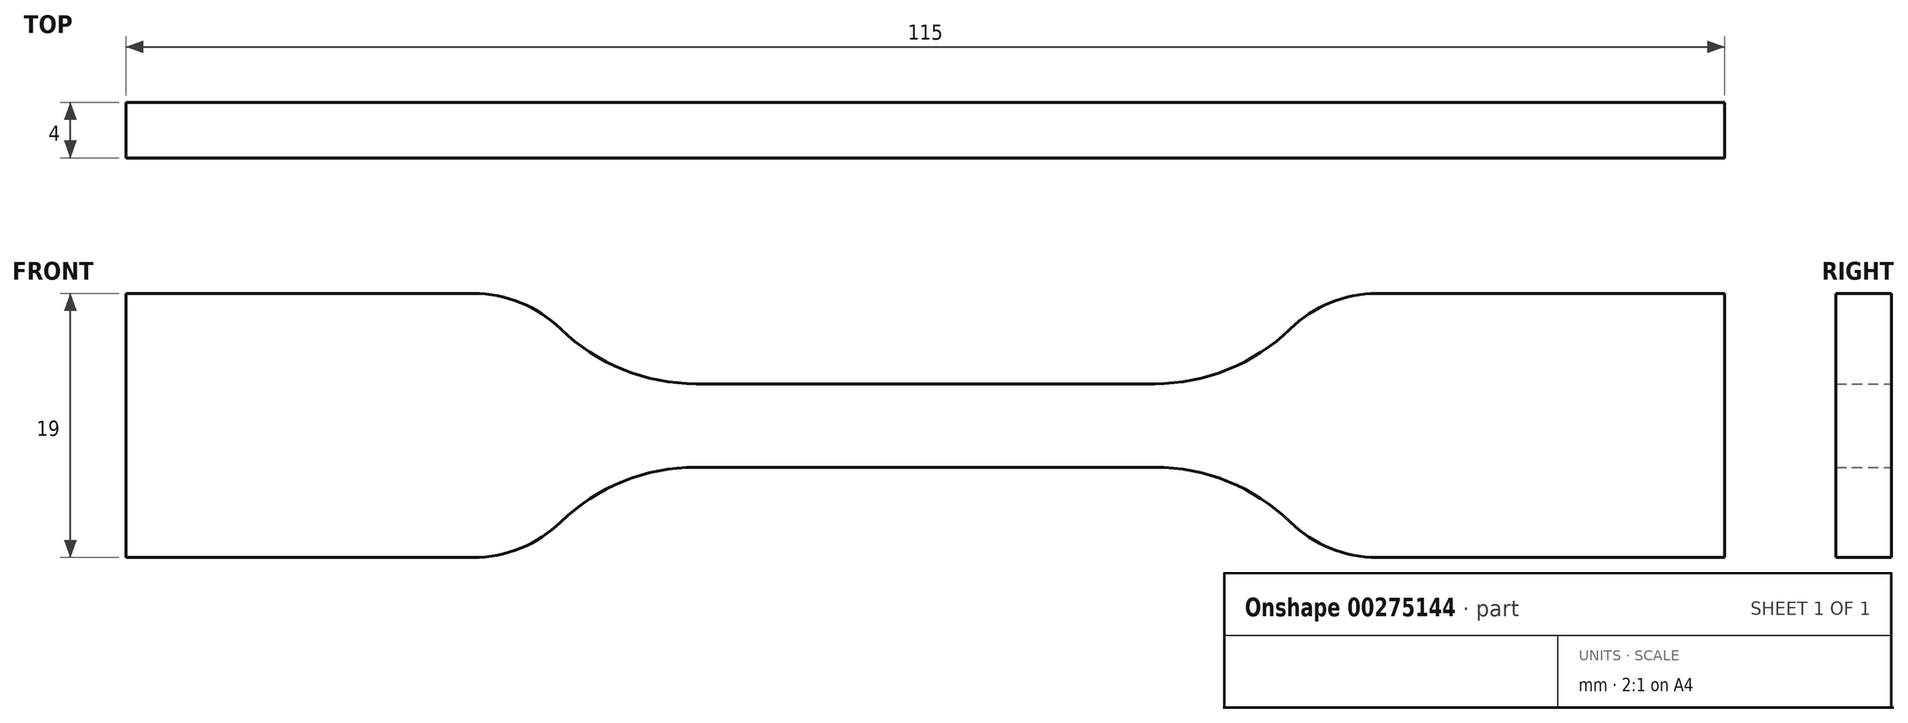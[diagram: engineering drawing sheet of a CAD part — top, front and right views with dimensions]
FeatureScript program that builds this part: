
annotation { "Feature Type Name" : "Feature", "Feature Type Description" : "" }
export const myFeature = defineFeature(function(context is Context, id is Id, definition is map)
    precondition{}
    {
        {
            var Q0;
            Q0=qCreatedBy(makeId("Front.planeOp"),FACE);
            var sketch = newSketch(context, id + "F0", { "sketchPlane" : qUnion([Q0])});
            skLineSegment(sketch, "E0", {"start": v(0, 3) * mm, "end": v(16.5, 3) * mm});
            skArc(sketch, "E1", {"start": v(16.5, 3) * mm, "mid": v(21.75, 4.02) * mm, "end": v(26.24, 6.94) * mm});
            skLineSegment(sketch, "E2", {"start": v(32.5, 9.5) * mm, "end": v(57.5, 9.5) * mm});
            skLineSegment(sketch, "E3", {"start": v(57.5, 9.5) * mm, "end": v(57.5, 0) * mm});
            skArc(sketch, "E4", {"start": v(32.5, 9.5) * mm, "mid": v(29.12, 8.84) * mm, "end": v(26.24, 6.94) * mm});
            skLineSegment(sketch, "E5.MirrorCS", {"start": v(0, -3) * mm, "end": v(16.5, -3) * mm});
            skArc(sketch, "E6.MirrorCS", {"start": v(32.5, -9.5) * mm, "mid": v(29.12, -8.84) * mm, "end": v(26.24, -6.94) * mm});
            skLineSegment(sketch, "E7.MirrorCS", {"start": v(32.5, -9.5) * mm, "end": v(57.5, -9.5) * mm});
            skLineSegment(sketch, "E8.MirrorCS", {"start": v(57.5, -9.5) * mm, "end": v(57.5, 0) * mm});
            skArc(sketch, "E9.MirrorCS", {"start": v(16.5, -3) * mm, "mid": v(21.75, -4.02) * mm, "end": v(26.24, -6.94) * mm});
            skLineSegment(sketch, "E10.MirrorCS", {"start": v(-32.5, -9.5) * mm, "end": v(-57.5, -9.5) * mm});
            skLineSegment(sketch, "E11.MirrorCS", {"start": v(-32.5, 9.5) * mm, "end": v(-57.5, 9.5) * mm});
            skLineSegment(sketch, "E12.MirrorCS", {"start": v(0, -3) * mm, "end": v(-16.5, -3) * mm});
            skArc(sketch, "E13.MirrorCS", {"start": v(-32.5, -9.5) * mm, "mid": v(-29.12, -8.84) * mm, "end": v(-26.24, -6.94) * mm});
            skLineSegment(sketch, "E14.MirrorCS", {"start": v(-57.5, -9.5) * mm, "end": v(-57.5, 0) * mm});
            skArc(sketch, "E15.MirrorCS", {"start": v(-16.5, -3) * mm, "mid": v(-21.75, -4.02) * mm, "end": v(-26.24, -6.94) * mm});
            skLineSegment(sketch, "E16.MirrorCS", {"start": v(-57.5, 9.5) * mm, "end": v(-57.5, 0) * mm});
            skLineSegment(sketch, "E17.MirrorCS", {"start": v(0, 3) * mm, "end": v(-16.5, 3) * mm});
            skArc(sketch, "E18.MirrorCS", {"start": v(-32.5, 9.5) * mm, "mid": v(-29.12, 8.84) * mm, "end": v(-26.24, 6.94) * mm});
            skArc(sketch, "E19.MirrorCS", {"start": v(-16.5, 3) * mm, "mid": v(-21.75, 4.02) * mm, "end": v(-26.24, 6.94) * mm});
            skSolve(sketch);
        }
        {
            var Q0;
            Q0 = qSketchRegion(id + "F0", true);
            extrude(context, id + "F1", {"entities" : qUnion([Q0]), "endBound" : BoundingType.SYMMETRIC, "depth" : 4 * mm});
        }
    });
